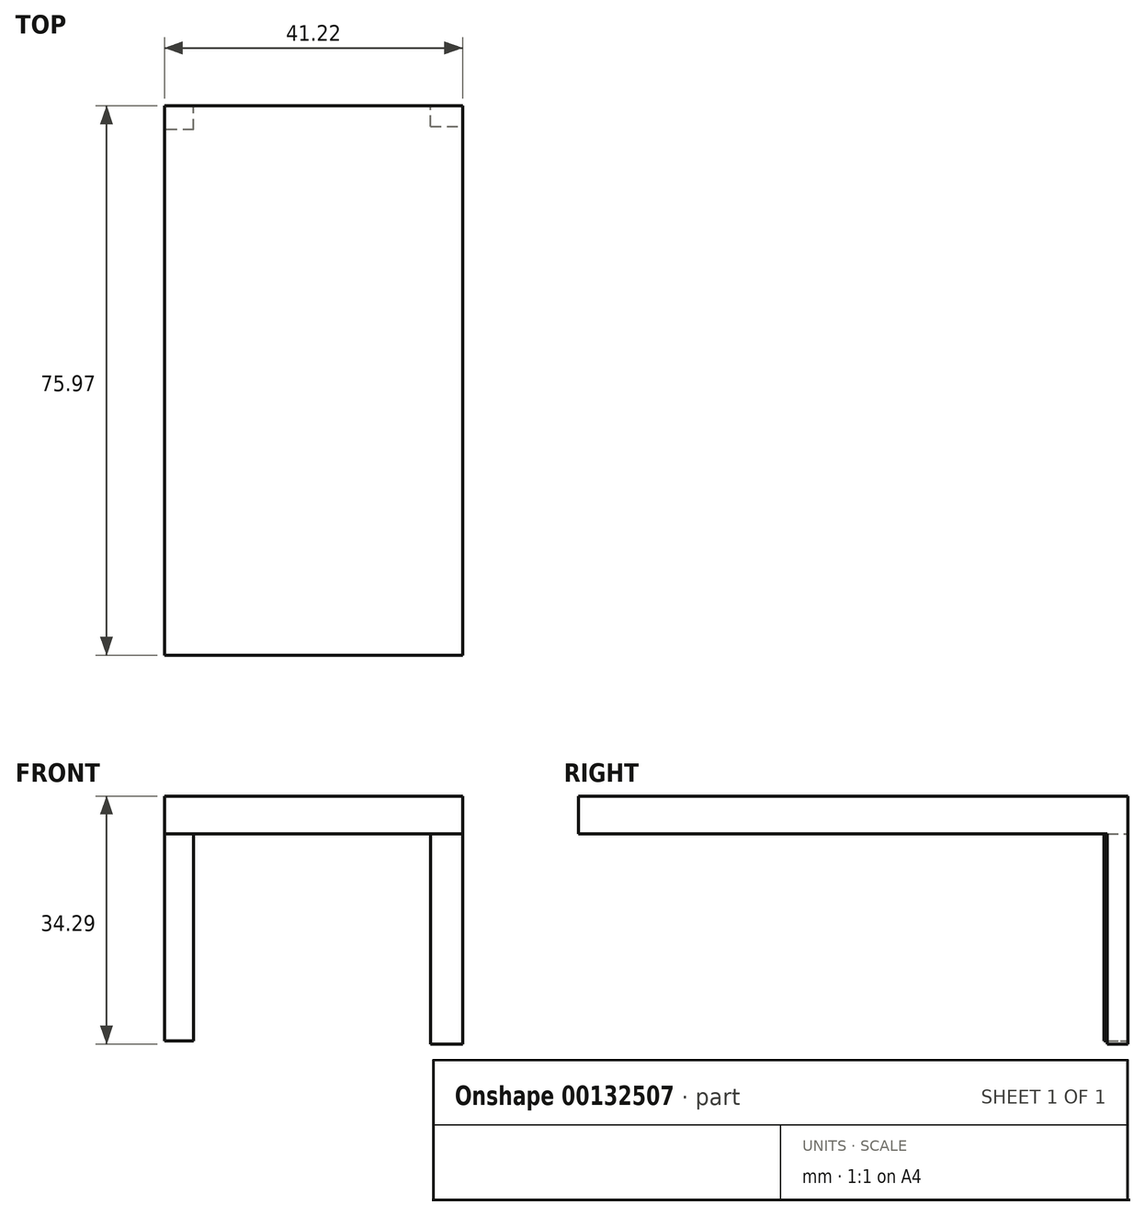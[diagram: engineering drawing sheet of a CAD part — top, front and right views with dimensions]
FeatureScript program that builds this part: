
annotation { "Feature Type Name" : "Feature", "Feature Type Description" : "" }
export const myFeature = defineFeature(function(context is Context, id is Id, definition is map)
    precondition{}
    {
        {
            var Q0;
            Q0=qCreatedBy(makeId("Top.planeOp"),FACE);
            var sketch = newSketch(context, id + "F0", { "sketchPlane" : qUnion([Q0])});
            skLineSegment(sketch, "E0", {"start": v(0, 0) * mm, "end": v(0, -75.97) * mm});
            skLineSegment(sketch, "E1", {"start": v(0, -75.97) * mm, "end": v(41.22, -75.97) * mm});
            skLineSegment(sketch, "E2", {"start": v(41.22, -75.97) * mm, "end": v(41.22, 0) * mm});
            skLineSegment(sketch, "E3", {"start": v(41.22, 0) * mm, "end": v(0, 0) * mm});
            skSolve(sketch);
        }
        {
            var Q0;
            Q0=makeQuery(id+"F0.imprint","IMPRINT",FACE,{"disambiguationData":[TD([[makeQuery(id+"F0.imprint","IMPRINT",EDGE,{"derivedFrom":sQuery(id+"F0.wireOp",EDGE,"E0")}),1.0]])]});
            extrude(context, id + "F1", {"entities" : qUnion([Q0]), "depth" : 5.2 * mm});
        }
        {
            var Q0;
            Q0=qCreatedBy(makeId("Front.planeOp"),FACE);
            var sketch = newSketch(context, id + "F2", { "sketchPlane" : qUnion([Q0])});
            skLineSegment(sketch, "E4", {"start": v(0, 0) * mm, "end": v(0, -28.7) * mm});
            skLineSegment(sketch, "E5", {"start": v(0, -28.7) * mm, "end": v(4.04, -28.7) * mm});
            skLineSegment(sketch, "E6", {"start": v(4.04, -28.7) * mm, "end": v(4.04, 0) * mm});
            skLineSegment(sketch, "E7", {"start": v(4.04, 0) * mm, "end": v(0, 0) * mm});
            skLineSegment(sketch, "E8", {"start": v(39.8, 0) * mm, "end": v(39.8, -27.68) * mm});
            skLineSegment(sketch, "E9", {"start": v(39.8, -27.68) * mm, "end": v(35.76, -27.68) * mm});
            skLineSegment(sketch, "E10", {"start": v(35.76, -27.68) * mm, "end": v(35.76, 0) * mm});
            skSolve(sketch);
        }
        {
            var Q0;
            Q0 = qSketchRegion(id + "F2", true);
            extrude(context, id + "F3", {"entities" : qUnion([Q0]), "operationType" : NewBodyOperationType.ADD, "depth" : 3.31 * mm});
        }
        {
            var Q0;
            Q0=qCreatedBy(makeId("Front.planeOp"),FACE);
            var sketch = newSketch(context, id + "F4", { "sketchPlane" : qUnion([Q0])});
            skLineSegment(sketch, "E11", {"start": v(41.22, 0) * mm, "end": v(41.22, -29.1) * mm});
            skLineSegment(sketch, "E12", {"start": v(41.22, -29.1) * mm, "end": v(36.77, -29.1) * mm});
            skLineSegment(sketch, "E13", {"start": v(36.77, -29.1) * mm, "end": v(36.77, 0) * mm});
            skLineSegment(sketch, "E14", {"start": v(36.77, 0) * mm, "end": v(41.22, 0) * mm});
            skSolve(sketch);
        }
        {
            var Q0;
            Q0 = qSketchRegion(id + "F4", true);
            extrude(context, id + "F5", {"entities" : qUnion([Q0]), "operationType" : NewBodyOperationType.ADD, "depth" : 2.85 * mm});
        }
    });
